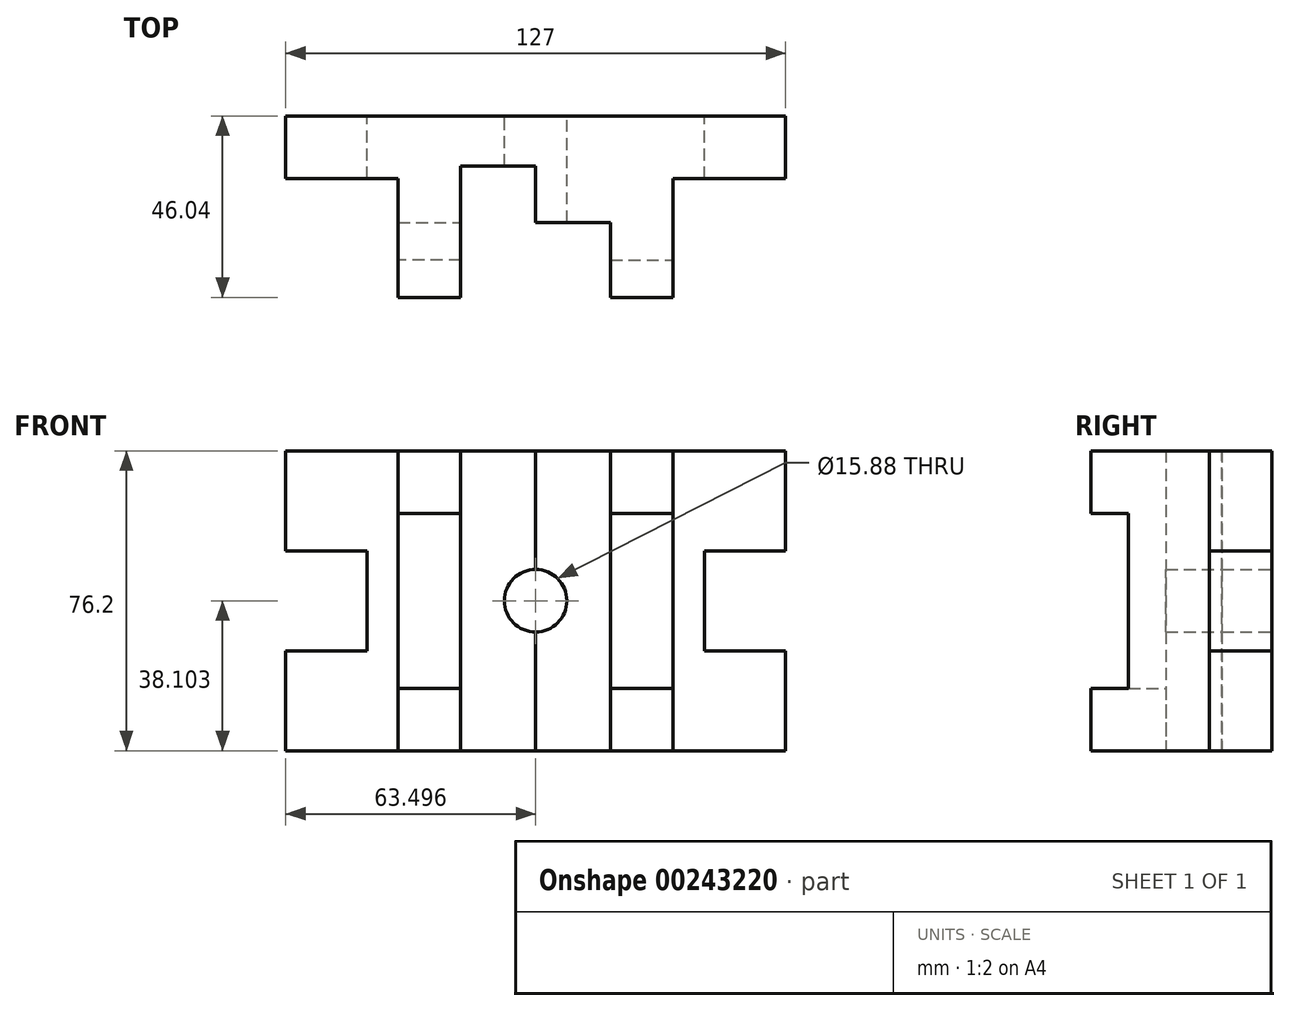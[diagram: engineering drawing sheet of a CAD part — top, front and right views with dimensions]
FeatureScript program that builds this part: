
annotation { "Feature Type Name" : "Feature", "Feature Type Description" : "" }
export const myFeature = defineFeature(function(context is Context, id is Id, definition is map)
    precondition{}
    {
        {
            var Q0;
            Q0=qCreatedBy(makeId("Front.planeOp"),FACE);
            var sketch = newSketch(context, id + "F0", { "sketchPlane" : qUnion([Q0])});
            skLineSegment(sketch, "E0.bottom", {"start": v(-110.4, 89.52) * mm, "end": v(16.6, 89.52) * mm});
            skLineSegment(sketch, "E0.top", {"start": v(-110.4, -62.88) * mm, "end": v(16.6, -62.88) * mm});
            skLineSegment(sketch, "E0.left", {"start": v(-110.4, 89.52) * mm, "end": v(-110.4, 38.72) * mm});
            skLineSegment(sketch, "E0.right", {"start": v(16.6, 89.52) * mm, "end": v(16.6, 29.2) * mm});
            skLineSegment(sketch, "E1", {"start": v(-110.4, -62.88) * mm, "end": v(-110.4, -12.08) * mm});
            skLineSegment(sketch, "E2.bottom", {"start": v(-110.4, 38.72) * mm, "end": v(-69.12, 38.72) * mm});
            skLineSegment(sketch, "E2.top", {"start": v(-110.4, -12.08) * mm, "end": v(-69.12, -12.08) * mm});
            skLineSegment(sketch, "E2.right", {"start": v(-69.12, 38.72) * mm, "end": v(-69.12, -12.08) * mm});
            skLineSegment(sketch, "E3.trimOffspring", {"start": v(-110.4, -12.08) * mm, "end": v(-110.4, -62.88) * mm});
            skLineSegment(sketch, "E4", {"start": v(-110.4, 89.52) * mm, "end": v(-53.24, 89.52) * mm});
            skLineSegment(sketch, "E5", {"start": v(-110.4, -62.88) * mm, "end": v(-53.24, -62.88) * mm});
            skLineSegment(sketch, "E6", {"start": v(-53.24, 89.52) * mm, "end": v(-53.24, -62.88) * mm});
            skLineSegment(sketch, "E7", {"start": v(-53.24, -62.88) * mm, "end": v(-21.5, -62.88) * mm});
            skLineSegment(sketch, "E8", {"start": v(-21.5, -62.88) * mm, "end": v(-21.5, -57.01) * mm});
            skLineSegment(sketch, "E9", {"start": v(-21.5, -31.13) * mm, "end": v(-21.5, -62.88) * mm});
            skLineSegment(sketch, "E10", {"start": v(-21.5, -31.13) * mm, "end": v(-53.24, -31.13) * mm});
            skLineSegment(sketch, "E11.MirrorCS", {"start": v(-21.5, 57.77) * mm, "end": v(-53.24, 57.77) * mm});
            skLineSegment(sketch, "E12.MirrorCS", {"start": v(-21.5, 57.77) * mm, "end": v(-21.5, 89.52) * mm});
            skLineSegment(sketch, "E13", {"start": v(-21.5, 57.77) * mm, "end": v(-21.5, -31.13) * mm});
            skLineSegment(sketch, "E14", {"start": v(-21.5, 89.52) * mm, "end": v(0, 89.52) * mm});
            skArc(sketch, "E15", {"start": v(16.6, 29.2) * mm, "mid": v(0.73, 13.32) * mm, "end": v(16.6, -2.56) * mm});
            skArc(sketch, "E16.MirrorCS", {"start": v(16.6, 29.2) * mm, "mid": v(32.48, 13.32) * mm, "end": v(16.6, -2.56) * mm});
            skLineSegment(sketch, "E17.MirrorCS", {"start": v(54.7, 57.77) * mm, "end": v(54.7, -31.13) * mm});
            skLineSegment(sketch, "E18.MirrorCS", {"start": v(54.7, -31.13) * mm, "end": v(86.46, -31.13) * mm});
            skLineSegment(sketch, "E19.MirrorCS", {"start": v(86.46, 89.52) * mm, "end": v(86.46, -62.88) * mm});
            skLineSegment(sketch, "E20.MirrorCS", {"start": v(54.7, 57.77) * mm, "end": v(86.46, 57.77) * mm});
            skLineSegment(sketch, "E21.MirrorCS", {"start": v(143.6, 89.52) * mm, "end": v(16.6, 89.52) * mm});
            skLineSegment(sketch, "E22.MirrorCS", {"start": v(143.6, 89.52) * mm, "end": v(143.6, 38.72) * mm});
            skLineSegment(sketch, "E23.MirrorCS", {"start": v(143.6, -12.08) * mm, "end": v(102.33, -12.08) * mm});
            skLineSegment(sketch, "E24.MirrorCS", {"start": v(102.33, 38.72) * mm, "end": v(102.33, -12.08) * mm});
            skLineSegment(sketch, "E25.MirrorCS", {"start": v(143.6, -62.88) * mm, "end": v(86.46, -62.88) * mm});
            skLineSegment(sketch, "E26.MirrorCS", {"start": v(143.6, 38.72) * mm, "end": v(102.33, 38.72) * mm});
            skLineSegment(sketch, "E27.MirrorCS", {"start": v(54.7, -31.13) * mm, "end": v(54.7, -62.88) * mm});
            skLineSegment(sketch, "E28.MirrorCS", {"start": v(143.6, -62.88) * mm, "end": v(16.6, -62.88) * mm});
            skLineSegment(sketch, "E29.MirrorCS", {"start": v(143.6, -12.08) * mm, "end": v(143.6, -62.88) * mm});
            skLineSegment(sketch, "E30", {"start": v(54.7, 57.77) * mm, "end": v(54.7, 89.52) * mm});
            skLineSegment(sketch, "E31.trimOffspring", {"start": v(16.6, -2.56) * mm, "end": v(16.6, -62.88) * mm});
            skSolve(sketch);
        }
        {
            var Q0;
            Q0=makeQuery(id+"F0.imprint","IMPRINT",FACE,{"disambiguationData":[TD([[makeQuery(id+"F0.imprint","IMPRINT",EDGE,{"derivedFrom":sQuery(id+"F0.wireOp",EDGE,"E0.left")}),1.0]])]});
            var Q1;
            {var subQ5=sQuery(id+"F0.wireOp",EDGE,"E22.MirrorCS");Q1=makeQuery(id+"F0.imprint","IMPRINT",FACE,{"disambiguationData":[TD([[makeQuery(id+"F0.imprint","IMPRINT",EDGE,{"derivedFrom":subQ5}),-1.0]])]});}
            extrude(context, id + "F1", {"entities" : qUnion([Q0, Q1]), "depth" : 31.75 * mm});
        }
        {
            var Q0;
            {var subQ0=sQuery(id+"F0.wireOp",EDGE,"E18.MirrorCS");Q0=makeQuery(id+"F0.imprint","IMPRINT",FACE,{"disambiguationData":[TD([[makeQuery(id+"F0.imprint","IMPRINT",EDGE,{"derivedFrom":subQ0}),-1.0]])]});}
            var Q1;
            {var subQ1=sQuery(id+"F0.wireOp",EDGE,"E7");Q1=makeQuery(id+"F0.imprint","IMPRINT",FACE,{"disambiguationData":[TD([[makeQuery(id+"F0.imprint","IMPRINT",EDGE,{"derivedFrom":subQ1}),1.0]])]});}
            var Q2;
            {var subQ4=sQuery(id+"F0.wireOp",EDGE,"E11.MirrorCS");Q2=makeQuery(id+"F0.imprint","IMPRINT",FACE,{"disambiguationData":[TD([[makeQuery(id+"F0.imprint","IMPRINT",EDGE,{"derivedFrom":subQ4}),-1.0]])]});}
            var Q3;
            {var subQ0=sQuery(id+"F0.wireOp",EDGE,"E20.MirrorCS");Q3=makeQuery(id+"F0.imprint","IMPRINT",FACE,{"disambiguationData":[TD([[makeQuery(id+"F0.imprint","IMPRINT",EDGE,{"derivedFrom":subQ0}),1.0]])]});}
            extrude(context, id + "F2", {"entities" : qUnion([Q0, Q1, Q2, Q3]), "operationType" : NewBodyOperationType.ADD, "depth" : 92.07 * mm});
        }
        {
            var Q0;
            {var subQ1=sQuery(id+"F0.wireOp",EDGE,"E0.top");Q0=makeQuery(id+"F0.imprint","IMPRINT",FACE,{"disambiguationData":[TD([[makeQuery(id+"F0.imprint","IMPRINT",EDGE,{"derivedFrom":subQ1}),1.0]])]});}
            var Q1;
            {var subQ1=sQuery(id+"F0.wireOp",EDGE,"E0.right");Q1=makeQuery(id+"F0.imprint","IMPRINT",FACE,{"disambiguationData":[TD([[makeQuery(id+"F0.imprint","IMPRINT",EDGE,{"derivedFrom":subQ1}),1.0]])]});}
            extrude(context, id + "F3", {"entities" : qUnion([Q0, Q1]), "operationType" : NewBodyOperationType.ADD, "depth" : 53.97 * mm});
        }
        {
            var Q0;
            Q0 = qSketchRegion(id + "F0", true);
            extrude(context, id + "F4", {"entities" : qUnion([Q0]), "operationType" : NewBodyOperationType.ADD, "depth" : 25.4 * mm});
        }
        {
            var Q0;
            {var subQ0=sQuery(id+"F0.wireOp",EDGE,"E10");Q0=makeQuery(id+"F0.imprint","IMPRINT",FACE,{"disambiguationData":[TD([[makeQuery(id+"F0.imprint","IMPRINT",EDGE,{"derivedFrom":subQ0}),-1.0]])]});}
            extrude(context, id + "F5", {"entities" : qUnion([Q0]), "operationType" : NewBodyOperationType.ADD, "depth" : 73.02 * mm});
        }
        {
            var Q0;
            Q0=makeQuery(id+"F0.imprint","IMPRINT",FACE,{"disambiguationData":[TD([[makeQuery(id+"F0.imprint","IMPRINT",EDGE,{"derivedFrom":sQuery(id+"F0.wireOp",EDGE,"E17.MirrorCS")}),1.0]])]});
            extrude(context, id + "F6", {"entities" : qUnion([Q0]), "operationType" : NewBodyOperationType.ADD, "depth" : 73.02 * mm});
        }
        {
            var Q0;
            Q0=makeQuery(id+"F1.opExtrude","SWEPT_BODY",BODY,{"disambiguationData":[OSD([sQuery(id+"F0.wireOp",EDGE,"E0.left"),sQuery(id+"F0.wireOp",EDGE,"E2.bottom"),sQuery(id+"F0.wireOp",EDGE,"E2.top"),sQuery(id+"F0.wireOp",EDGE,"E2.right"),sQuery(id+"F0.wireOp",EDGE,"E3.trimOffspring"),sQuery(id+"F0.wireOp",EDGE,"E4"),sQuery(id+"F0.wireOp",EDGE,"E5"),sQuery(id+"F0.wireOp",EDGE,"E6")])]});
            var Q1;
            Q1=makeQuery(id+"F2.opExtrude","CAP_VERTEX",VERTEX,{"disambiguationData":[OSD([sQuery(id+"F0.wireOp",EDGE,"E17.MirrorCS"),sQuery(id+"F0.wireOp",EDGE,"E20.MirrorCS"),sQuery(id+"F0.wireOp",EDGE,"E30")])],"isStart":false});
            transform(context, id + "F7", {"entities" : qUnion([Q0]), "transformType" : TransformType.SCALE_UNIFORMLY, "scale" : 0.5, "scalePoint" : qUnion([Q1]), "makeCopy" : false});
        }
    });
